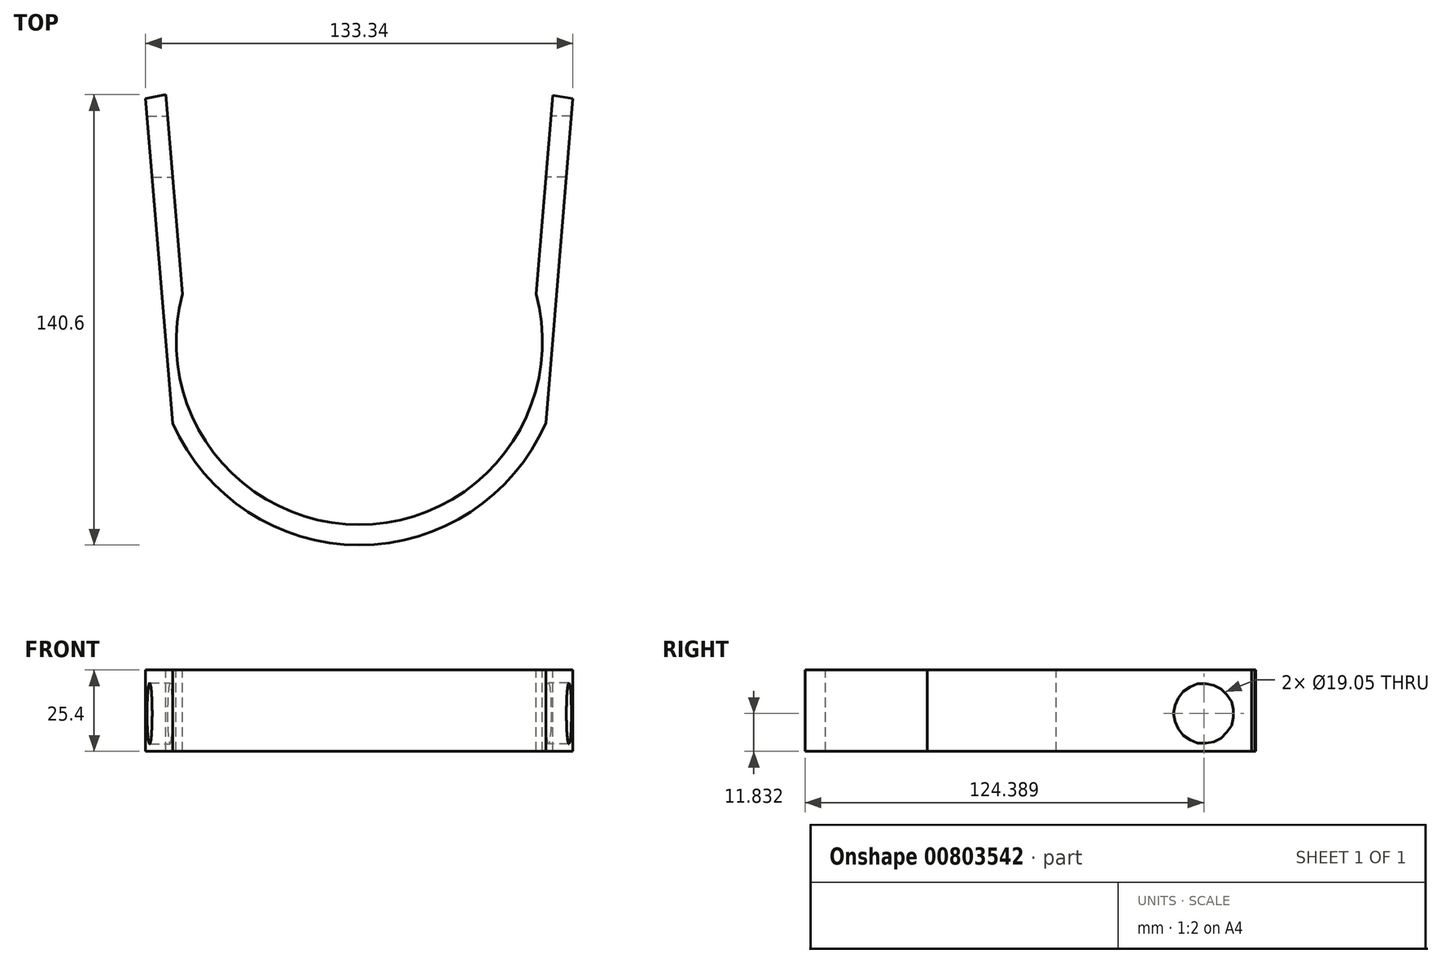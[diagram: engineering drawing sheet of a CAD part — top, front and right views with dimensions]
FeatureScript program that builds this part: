
annotation { "Feature Type Name" : "Feature", "Feature Type Description" : "" }
export const myFeature = defineFeature(function(context is Context, id is Id, definition is map)
    precondition{}
    {
        {
            var Q0;
            Q0=qCreatedBy(makeId("Top.planeOp"),FACE);
            var sketch = newSketch(context, id + "F0", { "sketchPlane" : qUnion([Q0])});
            skPoint(sketch, "E0.start.orphan", {"position": v(-32.54, 62.8) * mm});
            skPoint(sketch, "E1.start.orphan", {"position": v(86.2, 62.8) * mm});
            skLineSegment(sketch, "E2", {"start": v(-66.67, 73.26) * mm, "end": v(-58.19, -27.99) * mm});
            skLineSegment(sketch, "E3.MirrorCS", {"start": v(66.68, 73.26) * mm, "end": v(58.19, -27.99) * mm});
            skArc(sketch, "E4", {"start": v(-58.19, -27.99) * mm, "mid": v(0, -66.06) * mm, "end": v(58.19, -27.99) * mm});
            skLineSegment(sketch, "E5.0", {"start": v(60.39, 74.28) * mm, "end": v(55.19, 12.28) * mm});
            skArc(sketch, "E5.1", {"start": v(-55.19, 12.28) * mm, "mid": v(0, -59.7) * mm, "end": v(55.19, 12.28) * mm});
            skLineSegment(sketch, "E5.2", {"start": v(-60.41, 74.54) * mm, "end": v(-55.19, 12.28) * mm});
            skLineSegment(sketch, "E6", {"start": v(-66.68, 73.26) * mm, "end": v(-60.41, 74.54) * mm});
            skLineSegment(sketch, "E7", {"start": v(60.39, 74.28) * mm, "end": v(66.68, 73.26) * mm});
            skSolve(sketch);
        }
        {
            var Q0;
            Q0 = qSketchRegion(id + "F0", true);
            extrude(context, id + "F1", {"entities" : qUnion([Q0]), "oppositeDirection" : true, "depth" : 25.4 * mm, "offsetDistance" : 25.4 * mm});
        }
        {
            var Q0;
            Q0=qCreatedBy(makeId("Right.planeOp"),FACE);
            var sketch = newSketch(context, id + "F2", { "sketchPlane" : qUnion([Q0])});
            skCircle(sketch, "E8", {"center": v(58.33, -13.57) * mm, "radius": 9.53 * mm});
            skSolve(sketch);
        }
        {
            var Q0;
            Q0=makeQuery(id+"F2.imprint","IMPRINT",FACE,{"disambiguationData":[TD([[makeQuery(id+"F2.imprint","IMPRINT",EDGE,{"derivedFrom":sQuery(id+"F2.wireOp",EDGE,"E8")}),1.0]])]});
            extrude(context, id + "F3", {"entities" : qUnion([Q0]), "operationType" : NewBodyOperationType.REMOVE, "endBound" : BoundingType.THROUGH_ALL, "depth" : 25.4 * mm, "offsetDistance" : 25.4 * mm});
        }
        {
            var Q0;
            Q0 = qSketchRegion(id + "F2", true);
            extrude(context, id + "F4", {"entities" : qUnion([Q0]), "operationType" : NewBodyOperationType.REMOVE, "endBound" : BoundingType.THROUGH_ALL, "oppositeDirection" : true, "depth" : 25.4 * mm, "offsetDistance" : 25.4 * mm});
        }
    });
